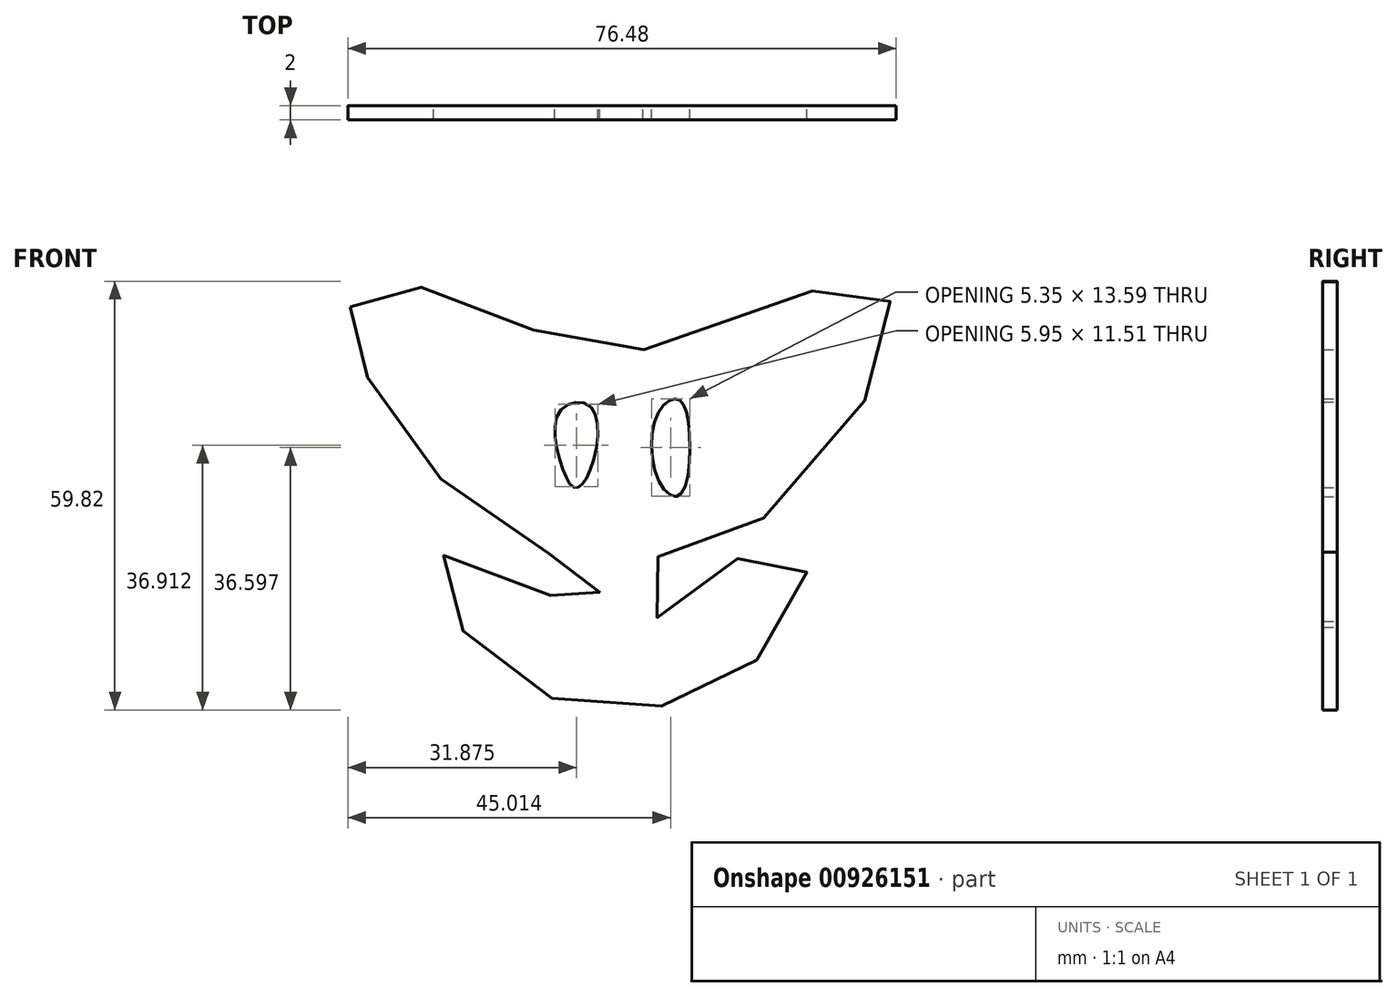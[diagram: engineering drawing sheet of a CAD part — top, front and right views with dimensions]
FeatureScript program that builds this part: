
annotation { "Feature Type Name" : "Feature", "Feature Type Description" : "" }
export const myFeature = defineFeature(function(context is Context, id is Id, definition is map)
    precondition{}
    {
        {
            var Q0;
            Q0=qCreatedBy(makeId("Front.planeOp"),FACE);
            var sketch = newSketch(context, id + "F0", { "sketchPlane" : qUnion([Q0])});
            skFitSpline(sketch, "E0", {"points": [v(-75.83, 56.25) * mm, v(-71.28, 59.72) * mm, v(-59.2, 56.25) * mm, v(-43.1, 51.15) * mm, v(-30.74, 50.88) * mm, v(-21.08, 55.17) * mm, v(-14.36, 57.32) * mm, v(-5.77, 59.72) * mm, v(0, 55.98) * mm, v(-4.16, 43.1) * mm, v(-22.15, 24.57) * mm, v(-33.7, 20.54) * mm, v(-34.23, 12.48) * mm, v(-29.4, 16.78) * mm, v(-18.4, 21.88) * mm, v(-12.48, 20.54) * mm, v(-15.17, 11.41) * mm, v(-25.1, 3.09) * mm, v(-37.92, 0) * mm, v(-51.95, 3.62) * mm, v(-61.89, 13.56) * mm, v(-63.77, 20.8) * mm, v(-52.76, 20) * mm, v(-42.02, 11.68) * mm, v(-41.75, 19.73) * mm, v(-44.7, 20.8) * mm, v(-58.13, 27.79) * mm, v(-71.55, 42.82) * mm, v(-75.83, 52.76) * mm, v(-75.83, 56.25) * mm]});
            skSolve(sketch);
        }
        {
            var Q0;
            Q0=makeQuery(id+"F0.imprint","IMPRINT",FACE,{"disambiguationData":[TD([[makeQuery(id+"F0.imprint","IMPRINT",EDGE,{"derivedFrom":sQuery(id+"F0.wireOp",EDGE,"E0")}),-1.0]])]});
            extrude(context, id + "F1", {"entities" : qUnion([Q0]), "depth" : 2 * mm, "offsetDistance" : 25.4 * mm});
        }
        {
            var Q0;
            Q0=makeQuery(id+"F1.opExtrude","CAP_FACE",FACE,{"disambiguationData":[OSD([sQuery(id+"F0.wireOp",EDGE,"E0")])],"isStart":false});
            var sketch = newSketch(context, id + "F2", { "sketchPlane" : qUnion([Q0])});
            skFitSpline(sketch, "E1", {"points": [v(-42.29, 42.29) * mm, v(-42.29, 33.7) * mm, v(-44.44, 31.01) * mm, v(-46.31, 33.96) * mm, v(-46.58, 41.75) * mm, v(-42.29, 42.29) * mm]});
            skFitSpline(sketch, "E2", {"points": [v(-32.9, 41.48) * mm, v(-32.9, 32.08) * mm, v(-29.94, 29.94) * mm, v(-28.6, 39.33) * mm, v(-30.2, 43.36) * mm, v(-32.9, 41.48) * mm]});
            skSolve(sketch);
        }
        {
            var Q0;
            Q0=makeQuery(id+"F2.imprint","IMPRINT",FACE,{"disambiguationData":[TD([[makeQuery(id+"F2.imprint","IMPRINT",EDGE,{"derivedFrom":sQuery(id+"F2.wireOp",EDGE,"E1")}),-1.0]])]});
            var Q1;
            Q1=makeQuery(id+"F2.imprint","IMPRINT",FACE,{"disambiguationData":[TD([[makeQuery(id+"F2.imprint","IMPRINT",EDGE,{"derivedFrom":sQuery(id+"F2.wireOp",EDGE,"E2")}),1.0]])]});
            extrude(context, id + "F3", {"entities" : qUnion([Q0, Q1]), "operationType" : NewBodyOperationType.REMOVE, "oppositeDirection" : true, "depth" : 25 * mm, "offsetDistance" : 25 * mm});
        }
    });
